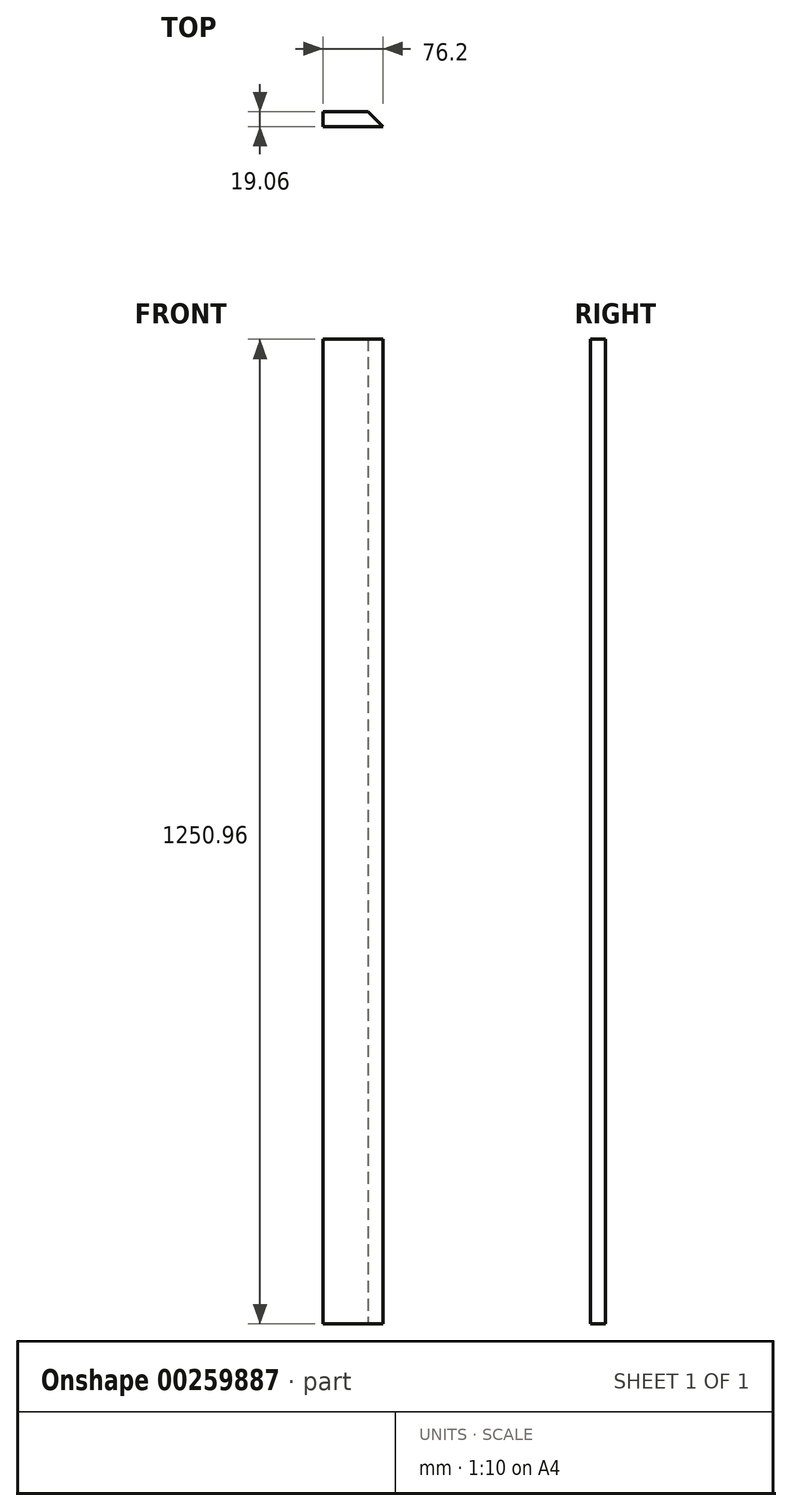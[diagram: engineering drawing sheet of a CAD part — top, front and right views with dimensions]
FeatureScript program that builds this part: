
annotation { "Feature Type Name" : "Feature", "Feature Type Description" : "" }
export const myFeature = defineFeature(function(context is Context, id is Id, definition is map)
    precondition{}
    {
        {
            var Q0;
            Q0=qCreatedBy(makeId("Top.planeOp"),FACE);
            var sketch = newSketch(context, id + "F0", { "sketchPlane" : qUnion([Q0])});
            skLineSegment(sketch, "E0.bottom", {"start": v(-38.1, 9.52) * mm, "end": v(38.1, 9.53) * mm});
            skLineSegment(sketch, "E0.top", {"start": v(-38.1, -9.53) * mm, "end": v(38.1, -9.52) * mm});
            skLineSegment(sketch, "E0.left", {"start": v(-38.1, 9.52) * mm, "end": v(-38.1, -9.53) * mm});
            skLineSegment(sketch, "E0.right", {"start": v(38.1, 9.53) * mm, "end": v(38.1, -9.52) * mm});
            skSolve(sketch);
        }
        {
            var Q0;
            Q0=makeQuery(id+"F0.imprint","IMPRINT",FACE,{"disambiguationData":[TD([[makeQuery(id+"F0.imprint","IMPRINT",EDGE,{"derivedFrom":sQuery(id+"F0.wireOp",EDGE,"E0.bottom")}),-1.0]])]});
            extrude(context, id + "F1", {"entities" : qUnion([Q0]), "endBound" : BoundingType.SYMMETRIC, "depth" : 1250.95 * mm});
        }
        {
            var Q0;
            Q0=makeQuery(id+"F1.opExtrude","SWEPT_EDGE",EDGE,{"disambiguationData":[OSD([sQuery(id+"F0.wireOp",EDGE,"E0.bottom"),sQuery(id+"F0.wireOp",EDGE,"E0.right")])]});
            chamfer(context, id + "F2", {"entities" : qUnion([Q0]), "chamferType" : ChamferType.OFFSET_ANGLE, "width" : 19.05 * mm, "oppositeDirection" : false, "angle" : 45 * degree, "tangentPropagation" : true});
        }
    });
